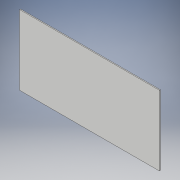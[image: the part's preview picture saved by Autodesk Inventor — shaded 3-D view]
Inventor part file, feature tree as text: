
AUTODESK INVENTOR PART (.ipt)
format: ipt  version: 2017 (Build 210142000, 142)  size: 88,576 bytes
history: native  units: in
note: dims shown in document units (in); Inventor stores cm internally (conversion verified against a paired STEP export)
features: extrude x1, sketch x1
ambient origin geometry x8: Origin, YZ Plane, XZ Plane, XY Plane, X Axis, Y Axis, Z Axis, Center Point
bodies: Solid1 (feature_tree)
feature tree (2):
  extrude  "Extrusion1"  Depth=36.0in
  sketch  "Sketch1"  dims[d0=72.0in d1=36.0in d2=0.5in d3=0.0in]
